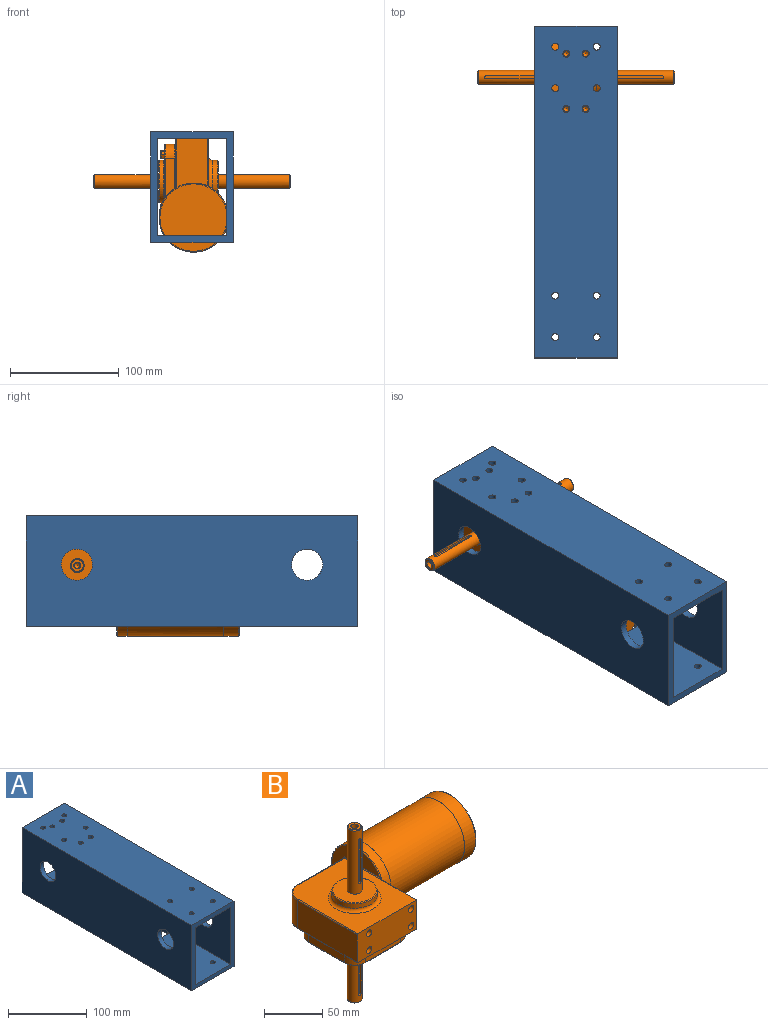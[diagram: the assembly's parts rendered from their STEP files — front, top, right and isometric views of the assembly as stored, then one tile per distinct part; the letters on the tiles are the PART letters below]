
ASSEMBLY  parts=2 mates=1
PART A: 46 faces, bbox 76.2x304.8x101.6 mm
  f0: plane 304.8x76.2mm, normal (0,0,-1), area 16249.9mm2, adj f4,f7,f8,f9,f26,f27,f28,f29
  f1: plane 304.8x63.5mm, normal (0,0,1), area 12379mm2, adj f5,f6,f8,f9,f26,f27,f28,f29
  f2: plane 304.8x76.2mm, normal (0,0,1), area 22845.7mm2, adj f4,f7,f8,f9,f14,f15,f16,f17
  f3: plane 304.8x63.5mm, normal (0,0,-1), area 18974.8mm2, adj f5,f6,f8,f9,f14,f15,f16,f17
  f4: plane 304.8x101.6mm, normal (-1,0,0), area 29685.1mm2, adj f0,f2,f8,f9,f12,f13
  f5: plane 304.8x88.9mm, normal (1,0,0), area 25814.1mm2, adj f1,f3,f8,f9,f12,f13
  f6: plane 304.8x88.9mm, normal (-1,0,0), area 25814.1mm2, adj f1,f3,f8,f9,f10,f11
  f7: plane 304.8x101.6mm, normal (1,0,0), area 29685.1mm2, adj f0,f2,f8,f9,f10,f11
  f8: plane 101.6x76.2mm, normal (0,-1,0), area 2096.8mm2, adj f0,f1,f2,f3,f4,f5,f6,f7
  f9: plane 101.6x76.2mm, normal (0,1,0), area 2096.8mm2, adj f0,f1,f2,f3,f4,f5,f6,f7
  f10: cylinder r=14.29mm len=28.58mm, axis (1,0,0), area 570mm2, adj f6,f7
  f11: cylinder r=14.29mm len=28.58mm, axis (1,0,0), area 570mm2, adj f6,f7
  f12: cylinder r=14.29mm len=28.58mm, axis (1,0,0), area 570mm2, adj f4,f5
  f13: cylinder r=14.29mm len=28.58mm, axis (1,0,0), area 570mm2, adj f4,f5
  f14: cylinder r=3.17mm len=6.35mm, axis (0,0,1), area 126.7mm2, adj f2,f3
  f15: cylinder r=3.17mm len=6.35mm, axis (0,0,1), area 126.7mm2, adj f2,f3
  f16: cylinder r=3.17mm len=6.35mm, axis (0,0,1), area 126.7mm2, adj f2,f3
  f17: cylinder r=3.17mm len=6.35mm, axis (0,0,1), area 126.7mm2, adj f2,f3
  f18: cylinder r=3.17mm len=6.35mm, axis (0,0,1), area 126.7mm2, adj f2,f3
  f19: cylinder r=3.17mm len=6.35mm, axis (0,0,1), area 126.7mm2, adj f2,f3
  f20: cylinder r=3.17mm len=6.35mm, axis (0,0,1), area 126.7mm2, adj f2,f3
  f21: cylinder r=3.17mm len=6.35mm, axis (0,0,1), area 126.7mm2, adj f2,f3
  f22: cylinder r=3.17mm len=6.35mm, axis (0,0,1), area 126.7mm2, adj f2,f3
  f23: cylinder r=3.17mm len=6.35mm, axis (0,0,1), area 126.7mm2, adj f2,f3
  f24: cylinder r=3.17mm len=6.35mm, axis (0,0,1), area 126.7mm2, adj f2,f3
  f25: cylinder r=3.17mm len=6.35mm, axis (0,0,1), area 126.7mm2, adj f2,f3
  f26: cylinder r=3.17mm len=6.35mm, axis (0,0,1), area 126.7mm2, adj f0,f1
  f27: cylinder r=3.17mm len=6.35mm, axis (0,0,1), area 126.7mm2, adj f0,f1
  f28: cylinder r=3.17mm len=6.35mm, axis (0,0,1), area 126.7mm2, adj f0,f1
  f29: cylinder r=3.17mm len=6.35mm, axis (0,0,1), area 126.7mm2, adj f0,f1
  f30: cylinder r=3.17mm len=6.35mm, axis (0,0,1), area 126.7mm2, adj f0,f1
  f31: cylinder r=3.17mm len=6.35mm, axis (0,0,1), area 126.7mm2, adj f0,f1
  f32: cylinder r=3.17mm len=6.35mm, axis (0,0,1), area 126.7mm2, adj f0,f1
  f33: cylinder r=3.17mm len=6.35mm, axis (0,0,1), area 126.7mm2, adj f0,f1
  f34: cylinder r=3.17mm len=6.35mm, axis (0,0,1), area 126.7mm2, adj f0,f1
  f35: cylinder r=3.17mm len=6.35mm, axis (0,0,1), area 126.7mm2, adj f0,f1
  f36: cylinder r=3.17mm len=6.35mm, axis (0,0,1), area 126.7mm2, adj f0,f1
  f37: cylinder r=3.17mm len=6.35mm, axis (0,0,1), area 126.7mm2, adj f0,f1
  f38: plane 103.32x6.35mm, normal (-1,0,0), area 656.1mm2, adj f0,f1,f39,f45
  f39: cylinder r=6.35mm len=6.35mm, axis (0,0,-1), area 63.3mm2, adj f0,f1,f38,f40
  f40: plane 44.45x6.35mm, normal (0,1,0), area 282.3mm2, adj f0,f1,f39,f41
  f41: cylinder r=6.35mm len=6.35mm, axis (0,0,-1), area 63.3mm2, adj f0,f1,f40,f42
  f42: plane 103.32x6.35mm, normal (1,0,0), area 656.1mm2, adj f0,f1,f41,f43
  f43: cylinder r=6.35mm len=6.35mm, axis (0,0,-1), area 63.3mm2, adj f0,f1,f42,f44
  f44: plane 44.45x6.35mm, normal (0,-1,0), area 282.3mm2, adj f0,f1,f43,f45
  f45: cylinder r=6.35mm len=6.35mm, axis (0,0,-1), area 63.3mm2, adj f0,f1,f38,f44
PART B: 156 faces, bbox 186.3x106.8x181.6 mm
  f0: plane 66.97x66.97mm, normal (0,0,-1), area 2932.5mm2, adj f42,f43,f44,f45,f46,f47,f48,f49
  f1: plane 63.5x63.5mm, normal (1,0,0), area 19mm2, adj f24,f26
  f2: plane 37.36x37.36mm, normal (0,0,-1), area 969.8mm2, adj f22,f61
  f3: plane 37.36x37.36mm, normal (0,0,1), area 969.8mm2, adj f21,f59
  f4: plane 87.47x70.8mm, normal (0,0,1), area 4532.6mm2, adj f7,f33,f36,f38,f41,f62,f67
  f5: plane 87.47x70.8mm, normal (0,0,-1), area 1380.8mm2, adj f7,f31,f32,f34,f35,f50,f51,f52
  f6: plane 72.39x28.89mm, normal (-1,0,0), area 2091.5mm2, adj f7,f30,f31,f33
  f7: plane 72.39x30.48mm, normal (0,-1,0), area 2079.2mm2, adj f4,f5,f6,f8,f31,f33,f66,f67
  f8: plane 44.93x28.89mm, normal (1,0,0), area 1208mm2, adj f7,f24,f66,f67
  f9: plane 55.72x28.89mm, normal (0,1,0), area 1609.9mm2, adj f30,f34,f38,f39
  f10: cylinder r=12.7mm len=12.7mm, axis (0,0,1), area 165.9mm2, adj f11,f17,f49,f57
  f11: plane 43.15x8.32mm, normal (0,1,0), area 359mm2, adj f10,f12,f48,f56
  f12: cylinder r=12.7mm len=12.7mm, axis (0,0,1), area 165.9mm2, adj f11,f13,f46,f54
  f13: plane 43.15x8.32mm, normal (1,0,0), area 359mm2, adj f12,f14,f44,f52
  f14: cylinder r=12.7mm len=12.7mm, axis (0,0,1), area 165.9mm2, adj f13,f15,f42,f50
  f15: plane 43.15x8.32mm, normal (0,-1,0), area 359mm2, adj f14,f16,f43,f51
  f16: cylinder r=12.7mm len=12.7mm, axis (0,0,1), area 165.9mm2, adj f15,f17,f45,f53
  f17: plane 43.15x8.32mm, normal (-1,0,0), area 359mm2, adj f10,f16,f47,f55
  f18: cylinder r=19.48mm len=38.95mm, axis (0,0,1), area 470.9mm2, adj f60,f61
  f19: cylinder r=19.48mm len=38.95mm, axis (0,0,1), area 574.2mm2, adj f59,f62
  f20: plane 11.11x11.11mm, normal (0,0,1), area 65.3mm2, adj f85,f93
  f21: cylinder r=6.35mm len=66.11mm, axis (0,0,-1), area 2497.1mm2, adj f3,f85,f94,f95,f96,f97
  f22: cylinder r=6.35mm len=59.43mm, axis (0,0,-1), area 2230.5mm2, adj f2,f84,f99,f100,f101,f102
  f23: plane 11.11x11.11mm, normal (0,0,-1), area 65.3mm2, adj f84,f89
  f24: cylinder r=31.75mm len=63.5mm, axis (-1,0,0), area 1767.6mm2, adj f1,f8,f63,f64,f65,f66,f67
  f25: plane 61.91x58.28mm, normal (-1,0,0), area 1532.1mm2, adj f35,f37,f39,f40,f41,f64
  f26: cylinder r=31.65mm len=88.9mm, axis (-1,0,0), area 17681.6mm2, adj f1,f27
  f27: plane 63.5x63.5mm, normal (-1,0,0), area 19mm2, adj f26,f28
  f28: cylinder r=31.75mm len=63.5mm, axis (-1,0,0), area 2679.2mm2, adj f27,f58
  f29: plane 61.91x61.91mm, normal (1,0,0), area 3010.6mm2, adj f58
  f30: cylinder r=15.88mm len=28.89mm, axis (0,0,-1), area 720.5mm2, adj f6,f9,f32,f36
  f31: cylinder r=0.79mm len=72.39mm, axis (0,1,0), area 90.3mm2, adj f5,f6,f7,f32
  f32: torus R=15.08mm, axis (0,0,-1), area 30.5mm2, adj f5,f30,f31,f34
  f33: cylinder r=0.79mm len=72.39mm, axis (0,-1,0), area 90.3mm2, adj f4,f6,f7,f36
  f34: cylinder r=0.79mm len=55.72mm, axis (1,0,0), area 69.5mm2, adj f5,f9,f32,f37
  f35: cylinder r=0.79mm len=41.62mm, axis (0,-1,0), area 51.3mm2, adj f5,f25,f37,f63
  f36: torus R=15.08mm, axis (0,0,-1), area 30.5mm2, adj f4,f30,f33,f38
  f37: torus R=1.59mm, axis (-1,0,0), area 2.1mm2, adj f25,f34,f35,f39
  f38: cylinder r=0.79mm len=55.72mm, axis (-1,0,0), area 69.5mm2, adj f4,f9,f36,f40
  f39: cylinder r=0.79mm len=28.89mm, axis (0,0,-1), area 36mm2, adj f9,f25,f37,f40
  f40: torus R=1.59mm, axis (-1,0,0), area 2.1mm2, adj f25,f38,f39,f41
  f41: cylinder r=0.79mm len=43.2mm, axis (0,1,0), area 53.4mm2, adj f4,f25,f40,f65
  f42: torus R=11.91mm, axis (0,0,1), area 24.3mm2, adj f0,f14,f43,f44
  f43: cylinder r=0.79mm len=43.15mm, axis (-1,0,0), area 53.8mm2, adj f0,f15,f42,f45
  f44: cylinder r=0.79mm len=43.15mm, axis (0,-1,0), area 53.8mm2, adj f0,f13,f42,f46
  f45: torus R=11.91mm, axis (0,0,1), area 24.3mm2, adj f0,f16,f43,f47
  f46: torus R=11.91mm, axis (0,0,1), area 24.3mm2, adj f0,f12,f44,f48
  f47: cylinder r=0.79mm len=43.15mm, axis (0,1,0), area 53.8mm2, adj f0,f17,f45,f49
  f48: cylinder r=0.79mm len=43.15mm, axis (1,0,0), area 53.8mm2, adj f0,f11,f46,f49
  f49: torus R=11.91mm, axis (0,0,1), area 24.3mm2, adj f0,f10,f47,f48
  f50: torus R=13.49mm, axis (0,0,-1), area 25.4mm2, adj f5,f14,f51,f52
  f51: cylinder r=0.79mm len=43.15mm, axis (-1,0,0), area 53.8mm2, adj f5,f15,f50,f53
  f52: cylinder r=0.79mm len=43.15mm, axis (0,-1,0), area 53.8mm2, adj f5,f13,f50,f54
  f53: torus R=13.49mm, axis (0,0,-1), area 25.4mm2, adj f5,f16,f51,f55
  f54: torus R=13.49mm, axis (0,0,-1), area 25.4mm2, adj f5,f12,f52,f56
  f55: cylinder r=0.79mm len=43.15mm, axis (0,1,0), area 53.8mm2, adj f5,f17,f53,f57
  f56: cylinder r=0.79mm len=43.15mm, axis (1,0,0), area 53.8mm2, adj f5,f11,f54,f57
  f57: torus R=13.49mm, axis (0,0,-1), area 25.4mm2, adj f5,f10,f55,f56
  f58: torus R=30.96mm, axis (1,0,0), area 246.5mm2, adj f28,f29
  f59: torus R=18.68mm, axis (0,0,-1), area 150.3mm2, adj f3,f19
  f60: torus R=20.27mm, axis (0,0,1), area 154.8mm2, adj f0,f18
  f61: torus R=18.68mm, axis (0,0,-1), area 150.3mm2, adj f2,f18
  f62: torus R=22.65mm, axis (0,0,-1), area 646.4mm2, adj f4,f19
  f63: bspline ~1.78x1.75mm, area 1.9mm2, adj f24,f35,f64,f66
  f64: torus R=30.96mm, axis (-1,0,0), area 203.7mm2, adj f24,f25,f63,f65
  f65: bspline ~1.87x1.74mm, area 1.8mm2, adj f24,f41,f64,f67
  f66: cylinder r=0.79mm len=45.85mm, axis (0,-1,0), area 56.5mm2, adj f5,f7,f8,f24,f63
  f67: cylinder r=0.79mm len=44.27mm, axis (0,1,0), area 54.6mm2, adj f4,f7,f8,f24,f65
  f68: cone r=2.55mm half-angle=59deg, axis (0,-1,0), area 23.9mm2, adj f69
  f69: cylinder r=2.55mm len=5.11mm, axis (0,-1,0), area 61.1mm2, adj f68,f70
  f70: plane 6.35x6.35mm, normal (0,-1,0), area 11.2mm2, adj f69,f71
  f71: cylinder r=3.17mm len=12.7mm, axis (0,-1,0), area 253.4mm2, adj f7,f70
  f72: cone r=2.55mm half-angle=59deg, axis (0,-1,0), area 23.9mm2, adj f73
  f73: cylinder r=2.55mm len=5.11mm, axis (0,-1,0), area 61.1mm2, adj f72,f74
  f74: plane 6.35x6.35mm, normal (0,-1,0), area 11.2mm2, adj f73,f75
  f75: cylinder r=3.17mm len=12.7mm, axis (0,-1,0), area 253.4mm2, adj f7,f74
  f76: cone r=2.55mm half-angle=59deg, axis (0,-1,0), area 23.9mm2, adj f77
  f77: cylinder r=2.55mm len=5.11mm, axis (0,-1,0), area 61.1mm2, adj f76,f78
  f78: plane 6.35x6.35mm, normal (0,-1,0), area 11.2mm2, adj f77,f79
  f79: cylinder r=3.17mm len=12.7mm, axis (0,-1,0), area 253.4mm2, adj f7,f78
  f80: cone r=2.55mm half-angle=59deg, axis (0,-1,0), area 23.9mm2, adj f81
  f81: cylinder r=2.55mm len=5.11mm, axis (0,-1,0), area 61.1mm2, adj f80,f82
  f82: plane 6.35x6.35mm, normal (0,-1,0), area 11.2mm2, adj f81,f83
  f83: cylinder r=3.17mm len=12.7mm, axis (0,-1,0), area 253.4mm2, adj f7,f82
  f84: cone r=6.35mm half-angle=45deg, axis (0,0,1), area 42mm2, adj f22,f23
  f85: cone r=5.56mm half-angle=45deg, axis (0,0,-1), area 42mm2, adj f20,f21
  f86: cone r=2.55mm half-angle=59deg, axis (0,0,-1), area 23.9mm2, adj f87
  f87: cylinder r=2.55mm len=5.11mm, axis (0,0,-1), area 61.1mm2, adj f86,f88
  f88: plane 6.35x6.35mm, normal (0,0,-1), area 11.2mm2, adj f87,f89
  f89: cylinder r=3.17mm len=25.4mm, axis (0,0,-1), area 506.7mm2, adj f23,f88
  f90: cone r=2.55mm half-angle=59deg, axis (0,0,1), area 23.9mm2, adj f91
  f91: cylinder r=2.55mm len=5.11mm, axis (0,0,1), area 61.1mm2, adj f90,f92
  f92: plane 6.35x6.35mm, normal (0,0,1), area 11.2mm2, adj f91,f93
  f93: cylinder r=3.17mm len=25.4mm, axis (0,0,1), area 506.7mm2, adj f20,f92
  f94: cylinder r=1.59mm len=3.18mm, axis (0,-1,0), area 9.1mm2, adj f21,f95,f97,f98
  f95: plane 43.82x1.83mm, normal (-1,0,0), area 80.2mm2, adj f21,f94,f96,f98
  f96: cylinder r=1.59mm len=3.18mm, axis (0,-1,0), area 9.1mm2, adj f21,f95,f97,f98
  f97: plane 43.82x1.83mm, normal (1,0,0), area 80.2mm2, adj f21,f94,f96,f98
  f98: plane 46.99x3.18mm, normal (0,-1,0), area 147mm2, adj f94,f95,f96,f97
  f99: cylinder r=1.59mm len=3.18mm, axis (0,-1,0), area 9.1mm2, adj f22,f100,f102,f103
  f100: plane 43.82x1.83mm, normal (-1,0,0), area 80.2mm2, adj f22,f99,f101,f103
  f101: cylinder r=1.59mm len=3.18mm, axis (0,-1,0), area 9.1mm2, adj f22,f100,f102,f103
  f102: plane 43.82x1.83mm, normal (1,0,0), area 80.2mm2, adj f22,f99,f101,f103
  f103: plane 46.99x3.18mm, normal (0,-1,0), area 147mm2, adj f99,f100,f101,f102
  f104: plane 3.26x3.18mm, normal (0.87,-0.5,0), area 12mm2, adj f0,f105,f109,f148
  f105: plane 3.67x3.26mm, normal (0,-1,0), area 12mm2, adj f0,f104,f106,f146
  f106: plane 3.26x3.18mm, normal (-0.87,-0.5,0), area 12mm2, adj f0,f105,f107,f144
  f107: plane 3.26x3.18mm, normal (-0.87,0.5,0), area 12mm2, adj f0,f106,f108,f145
  f108: plane 3.67x3.26mm, normal (0,1,0), area 12mm2, adj f0,f107,f109,f147
  f109: plane 3.26x3.18mm, normal (0.87,0.5,0), area 12mm2, adj f0,f104,f108,f149
  f110: plane 7.04x6.1mm, normal (0,0,-1), area 32.2mm2, adj f144,f145,f146,f147,f148,f149
  f111: plane 3.26x3.18mm, normal (0.5,-0.87,0), area 12mm2, adj f0,f112,f116,f154
  f112: plane 3.26x3.18mm, normal (-0.5,-0.87,0), area 12mm2, adj f0,f111,f113,f152
  f113: plane 3.67x3.26mm, normal (-1,0,0), area 12mm2, adj f0,f112,f114,f150
  f114: plane 3.26x3.18mm, normal (-0.5,0.87,0), area 12mm2, adj f0,f113,f115,f151
  f115: plane 3.26x3.18mm, normal (0.5,0.87,0), area 12mm2, adj f0,f114,f116,f153
  f116: plane 3.67x3.26mm, normal (1,0,0), area 12mm2, adj f0,f111,f115,f155
  f117: plane 7.04x6.1mm, normal (0,0,-1), area 32.2mm2, adj f150,f151,f152,f153,f154,f155
  f118: plane 3.26x3.18mm, normal (-0.5,-0.87,0), area 12mm2, adj f0,f119,f123,f142
  f119: plane 3.67x3.26mm, normal (-1,0,0), area 12mm2, adj f0,f118,f120,f140
  f120: plane 3.26x3.18mm, normal (-0.5,0.87,0), area 12mm2, adj f0,f119,f121,f138
  f121: plane 3.26x3.18mm, normal (0.5,0.87,0), area 12mm2, adj f0,f120,f122,f139
  f122: plane 3.67x3.26mm, normal (1,0,0), area 12mm2, adj f0,f121,f123,f141
  f123: plane 3.26x3.18mm, normal (0.5,-0.87,0), area 12mm2, adj f0,f118,f122,f143
  f124: plane 7.04x6.1mm, normal (0,0,-1), area 32.2mm2, adj f138,f139,f140,f141,f142,f143
  f125: plane 3.26x3.18mm, normal (-0.87,-0.5,0), area 12mm2, adj f0,f126,f130,f136
  f126: plane 3.26x3.18mm, normal (-0.87,0.5,0), area 12mm2, adj f0,f125,f127,f134
  f127: plane 3.67x3.26mm, normal (0,1,0), area 12mm2, adj f0,f126,f128,f132
  f128: plane 3.26x3.18mm, normal (0.87,0.5,0), area 12mm2, adj f0,f127,f129,f133
  f129: plane 3.26x3.18mm, normal (0.87,-0.5,0), area 12mm2, adj f0,f128,f130,f135
  f130: plane 3.67x3.26mm, normal (0,-1,0), area 12mm2, adj f0,f125,f129,f137
  f131: plane 7.04x6.1mm, normal (0,0,-1), area 32.2mm2, adj f132,f133,f134,f135,f136,f137
  f132: cylinder r=0.13mm len=3.67mm, axis (-1,0,0), area 0.7mm2, adj f127,f131,f133,f134
  f133: cylinder r=0.13mm len=3.24mm, axis (-0.5,0.87,0), area 0.7mm2, adj f128,f131,f132,f135
  f134: cylinder r=0.13mm len=3.24mm, axis (-0.5,-0.87,0), area 0.7mm2, adj f126,f131,f132,f136
  f135: cylinder r=0.13mm len=3.24mm, axis (0.5,0.87,0), area 0.7mm2, adj f129,f131,f133,f137
  f136: cylinder r=0.13mm len=3.24mm, axis (0.5,-0.87,0), area 0.7mm2, adj f125,f131,f134,f137
  f137: cylinder r=0.13mm len=3.67mm, axis (1,0,0), area 0.7mm2, adj f130,f131,f135,f136
  f138: cylinder r=0.13mm len=3.24mm, axis (-0.87,-0.5,0), area 0.7mm2, adj f120,f124,f139,f140
  f139: cylinder r=0.13mm len=3.24mm, axis (-0.87,0.5,0), area 0.7mm2, adj f121,f124,f138,f141
  f140: cylinder r=0.13mm len=3.67mm, axis (0,-1,0), area 0.7mm2, adj f119,f124,f138,f142
  f141: cylinder r=0.13mm len=3.67mm, axis (0,1,0), area 0.7mm2, adj f122,f124,f139,f143
  f142: cylinder r=0.13mm len=3.24mm, axis (0.87,-0.5,0), area 0.7mm2, adj f118,f124,f140,f143
  f143: cylinder r=0.13mm len=3.24mm, axis (0.87,0.5,0), area 0.7mm2, adj f123,f124,f141,f142
  f144: cylinder r=0.13mm len=3.24mm, axis (0.5,-0.87,0), area 0.7mm2, adj f106,f110,f145,f146
  f145: cylinder r=0.13mm len=3.24mm, axis (-0.5,-0.87,0), area 0.7mm2, adj f107,f110,f144,f147
  f146: cylinder r=0.13mm len=3.67mm, axis (1,0,0), area 0.7mm2, adj f105,f110,f144,f148
  f147: cylinder r=0.13mm len=3.67mm, axis (-1,0,0), area 0.7mm2, adj f108,f110,f145,f149
  f148: cylinder r=0.13mm len=3.24mm, axis (0.5,0.87,0), area 0.7mm2, adj f104,f110,f146,f149
  f149: cylinder r=0.13mm len=3.24mm, axis (-0.5,0.87,0), area 0.7mm2, adj f109,f110,f147,f148
  f150: cylinder r=0.13mm len=3.67mm, axis (0,-1,0), area 0.7mm2, adj f113,f117,f151,f152
  f151: cylinder r=0.13mm len=3.24mm, axis (-0.87,-0.5,0), area 0.7mm2, adj f114,f117,f150,f153
  f152: cylinder r=0.13mm len=3.24mm, axis (0.87,-0.5,0), area 0.7mm2, adj f112,f117,f150,f154
  f153: cylinder r=0.13mm len=3.24mm, axis (-0.87,0.5,0), area 0.7mm2, adj f115,f117,f151,f155
  f154: cylinder r=0.13mm len=3.24mm, axis (0.87,0.5,0), area 0.7mm2, adj f111,f117,f152,f155
  f155: cylinder r=0.13mm len=3.67mm, axis (0,1,0), area 0.7mm2, adj f116,f117,f153,f154
PLACE A t=(-101.88,39.98,-62.18)mm
PLACE B rot(axis=(-0.58,0.58,-0.58),120deg) t=(-119.02,29.18,-39.81)mm
MATE fastened B.f68 <-> A.f15  axis (0,0,1) through (-94.89,14.58,-39.81)mm
